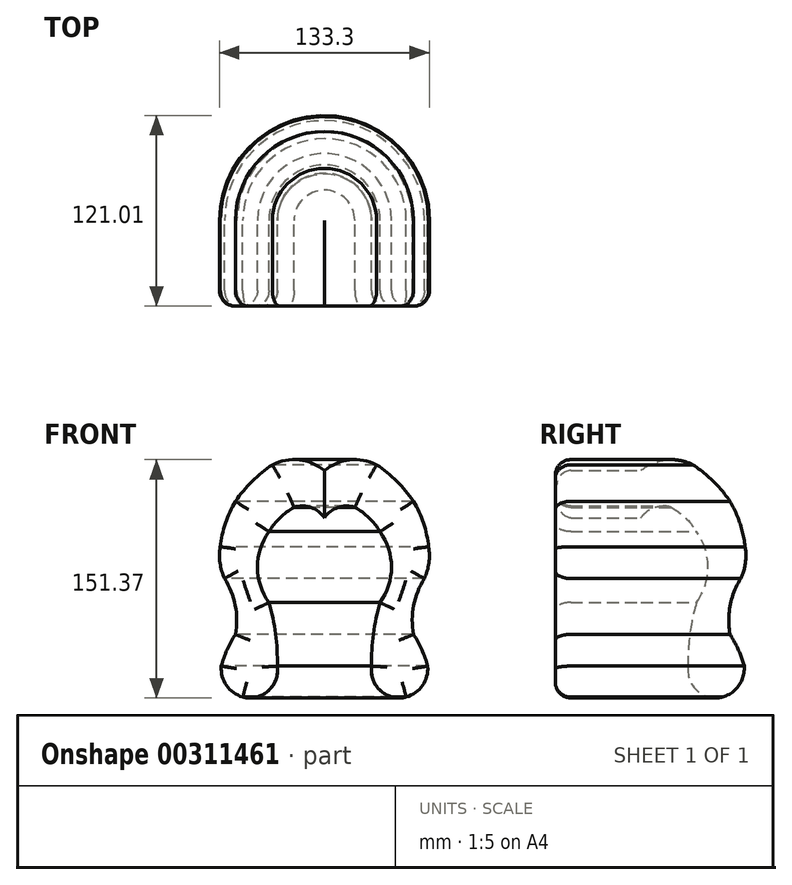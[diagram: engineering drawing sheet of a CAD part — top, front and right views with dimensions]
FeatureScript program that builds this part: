
annotation { "Feature Type Name" : "Feature", "Feature Type Description" : "" }
export const myFeature = defineFeature(function(context is Context, id is Id, definition is map)
    precondition{}
    {
        {
            var Q0;
            Q0=qCreatedBy(makeId("Front.planeOp"),FACE);
            var sketch = newSketch(context, id + "F0", { "sketchPlane" : qUnion([Q0])});
            skLineSegment(sketch, "E0", {"start": v(0, 28.58) * mm, "end": v(0, 48.43) * mm});
            skArc(sketch, "E1", {"start": v(0, 48.43) * mm, "mid": v(-16, 55.18) * mm, "end": v(-33.09, 52.04) * mm});
            skArc(sketch, "E2", {"start": v(-33.09, 52.04) * mm, "mid": v(-45.93, 41.58) * mm, "end": v(-56.55, 28.88) * mm});
            skArc(sketch, "E3", {"start": v(-56.55, 28.88) * mm, "mid": v(-62.91, 14.95) * mm, "end": v(-66.17, 0) * mm});
            skArc(sketch, "E4", {"start": v(-66.17, 0) * mm, "mid": v(-66.34, -10.28) * mm, "end": v(-63.47, -20.15) * mm});
            skArc(sketch, "E5", {"start": v(-56.55, -55.65) * mm, "mid": v(-56.67, -37.25) * mm, "end": v(-63.47, -20.15) * mm});
            skArc(sketch, "E6", {"start": v(-56.55, -55.65) * mm, "mid": v(-61.83, -65.38) * mm, "end": v(-65.57, -75.8) * mm});
            skArc(sketch, "E7", {"start": v(-65.57, -75.8) * mm, "mid": v(-62.23, -88.04) * mm, "end": v(-51.93, -95.46) * mm});
            skArc(sketch, "E8", {"start": v(-51.93, -95.46) * mm, "mid": v(-35.68, -91.51) * mm, "end": v(-29.96, -75.8) * mm});
            skArc(sketch, "E9", {"start": v(-29.96, -75.8) * mm, "mid": v(-31.04, -55.4) * mm, "end": v(-35.32, -35.43) * mm});
            skArc(sketch, "E10", {"start": v(-35.32, 9.58) * mm, "mid": v(-42.55, -12.92) * mm, "end": v(-35.32, -35.43) * mm});
            skArc(sketch, "E11", {"start": v(-19.3, 25.03) * mm, "mid": v(-28.3, 18.34) * mm, "end": v(-35.32, 9.58) * mm});
            skArc(sketch, "E12", {"start": v(0, 18.34) * mm, "mid": v(-8.5, 24.96) * mm, "end": v(-19.3, 25.03) * mm});
            skPoint(sketch, "E12.startSnap0", {"position": v(-28.3, 18.34) * mm});
            skLineSegment(sketch, "E13", {"start": v(0, 48.43) * mm, "end": v(0, 18.34) * mm});
            skSolve(sketch);
        }
        {
            var Q0;
            Q0=qCreatedBy(makeId("Front.planeOp"),FACE);
            var sketch = newSketch(context, id + "F1", { "sketchPlane" : qUnion([Q0])});
            skLineSegment(sketch, "E14", {"start": v(0, 51.83) * mm, "end": v(0, -61.22) * mm});
            skSolve(sketch);
        }
        {
            var Q0;
            {var subQ0=sQuery(id+"F0.wireOp",EDGE,"E1");Q0=makeQuery(id+"F0.imprint","IMPRINT",FACE,{"disambiguationData":[TD([[makeQuery(id+"F0.imprint","IMPRINT",EDGE,{"derivedFrom":subQ0}),1.0]])]});}
            var Q1;
            Q1=sQuery(id+"F1.wireOp",EDGE,"E14");
            revolve(context, id + "F2", {"entities" : qUnion([Q0]), "axis" : qUnion([Q1]), "revolveType" : RevolveType.ONE_DIRECTION, "angle" : 180 * degree});
        }
        {
            var Q0;
            Q0=makeQuery(id+"F2.opRevolve","CAP_FACE",FACE,{"disambiguationData":[OSD([sQuery(id+"F0.wireOp",EDGE,"E1"),sQuery(id+"F0.wireOp",EDGE,"E2"),sQuery(id+"F0.wireOp",EDGE,"E3"),sQuery(id+"F0.wireOp",EDGE,"E4"),sQuery(id+"F0.wireOp",EDGE,"E5"),sQuery(id+"F0.wireOp",EDGE,"E6"),sQuery(id+"F0.wireOp",EDGE,"E7"),sQuery(id+"F0.wireOp",EDGE,"E8"),sQuery(id+"F0.wireOp",EDGE,"E9"),sQuery(id+"F0.wireOp",EDGE,"E10"),sQuery(id+"F0.wireOp",EDGE,"E11"),sQuery(id+"F0.wireOp",EDGE,"E12"),sQuery(id+"F0.wireOp",EDGE,"E13")])],"isStart":false});
            extrude(context, id + "F3", {"entities" : qUnion([Q0]), "operationType" : NewBodyOperationType.ADD, "depth" : 33.78 * mm});
        }
        {
            var Q0;
            Q0=makeQuery(id+"F3.opExtrude","CAP_FACE",FACE,{"disambiguationData":[OSD([sQuery(id+"F0.wireOp",EDGE,"E1"),sQuery(id+"F0.wireOp",EDGE,"E2"),sQuery(id+"F0.wireOp",EDGE,"E3"),sQuery(id+"F0.wireOp",EDGE,"E4"),sQuery(id+"F0.wireOp",EDGE,"E5"),sQuery(id+"F0.wireOp",EDGE,"E6"),sQuery(id+"F0.wireOp",EDGE,"E7"),sQuery(id+"F0.wireOp",EDGE,"E8"),sQuery(id+"F0.wireOp",EDGE,"E9"),sQuery(id+"F0.wireOp",EDGE,"E10"),sQuery(id+"F0.wireOp",EDGE,"E11"),sQuery(id+"F0.wireOp",EDGE,"E12"),sQuery(id+"F0.wireOp",EDGE,"E13")])],"isStart":false});
            extrude(context, id + "F4", {"entities" : qUnion([Q0]), "operationType" : NewBodyOperationType.ADD, "depth" : 20.57 * mm});
        }
        {
            var Q0;
            Q0=makeQuery(id+"F4.opExtrude","CAP_FACE",FACE,{"disambiguationData":[OSD([sQuery(id+"F0.wireOp",EDGE,"E1"),sQuery(id+"F0.wireOp",EDGE,"E2"),sQuery(id+"F0.wireOp",EDGE,"E3"),sQuery(id+"F0.wireOp",EDGE,"E4"),sQuery(id+"F0.wireOp",EDGE,"E5"),sQuery(id+"F0.wireOp",EDGE,"E6"),sQuery(id+"F0.wireOp",EDGE,"E7"),sQuery(id+"F0.wireOp",EDGE,"E8"),sQuery(id+"F0.wireOp",EDGE,"E9"),sQuery(id+"F0.wireOp",EDGE,"E10"),sQuery(id+"F0.wireOp",EDGE,"E11"),sQuery(id+"F0.wireOp",EDGE,"E12"),sQuery(id+"F0.wireOp",EDGE,"E13")])],"isStart":false});
            fillet(context, id + "F5", {"entities" : qUnion([Q0]), "radius" : 9.8 * mm, "tangentPropagation" : true, "allowEdgeOverflow" : false});
        }
    });
